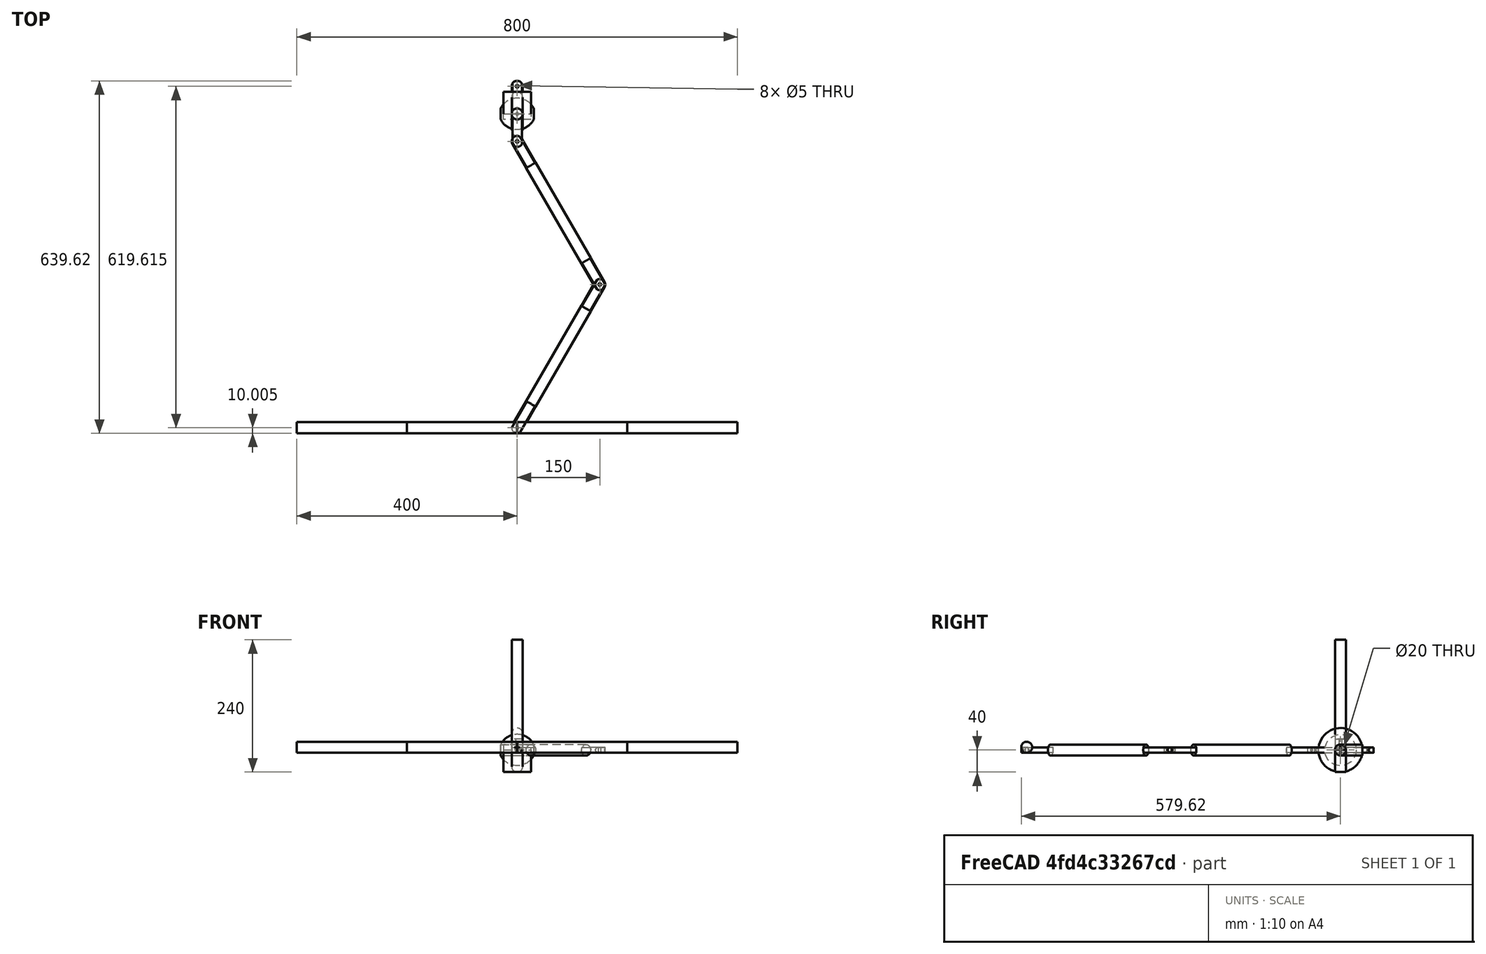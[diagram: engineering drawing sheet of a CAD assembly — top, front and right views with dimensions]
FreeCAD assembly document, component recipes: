
FREECAD ASSEMBLY — COMPONENT RECIPES ("Demo9Rev-Trans")

This assembly document has 7 components, labeled P0..P6 below (a component is one placed body or linked part). 7 of them carry a construction recipe — the FreeCAD feature program that regenerates the part from scratch, quoted from this document or its linked companion documents; the rest are supplied as boundary geometry only. No exploded tour is included for this assembly.
COMPONENT P0 — recipe-attached ("Weight", modeled in this document).
Construction recipe (the document's own serialized feature program — sketch geometry with constraints, then the solid features built on it; lengths are millimeters unless a unit is written):

FEATURE [Sketcher::SketchObject] Sketch
  FullyConstrained = true
  MapMode = 5
  Support = -> [XY_Plane]
  sketch-geometry (2):
    g0: LineSegment StartX=-30 StartY=10 StartZ=0 EndX=30 EndY=10 EndZ=0
    g1: ArcOfCircle CenterX=0 CenterY=-5 CenterZ=0 NormalX=0 NormalY=0 NormalZ=1 AngleXU=0 Radius=33.541 StartAngle=0.463648 EndAngle=2.67795
  constraints (7):
    c: Horizontal(g0)
    c: DistanceY(g-1,g0) = 10
    c: DistanceX(g-1,g0) = 30
    c: PointOnObject(g1,g-2)
    c: DistanceY(g1,g-1) = 5
    c: Coincident(g1,g0)
    c: Coincident(g1,g0)
FEATURE [PartDesign::Revolution] Revolution
  Angle = 360
  Axis = (1,0,0)
  Base = (0,0,0)
  Profile = -> Sketch
  ReferenceAxis = -> Sketch [H_Axis]
FEATURE [PartDesign::CoordinateSystem] WeightTop
  AttacherType = Attacher::AttachEngine3D
  MapMode = 11
  Placement = pos=(30,-1.8e-15,0) rot=(0.707107,0,0.707107;3.14159rad)
  Support = -> [Revolution]
FEATURE [PartDesign::CoordinateSystem] WeightBot
  AttacherType = Attacher::AttachEngine3D
  MapMode = 11
  Placement = pos=(-30,0,0) rot=(0.707107,0,0.707107;3.14159rad)
  Support = -> [Revolution]
FEATURE [PartDesign::CoordinateSystem] WeightLCS
  AttacherType = Attacher::AttachEngine3D
  MapMode = 2
  Support = -> [Body003]
FEATURE [PartDesign::Body] Body  label="Weight"
  Group = -> [Sketch,Revolution,WeightLCS,WeightTop,WeightBot]
  Origin = -> Origin
  Tip = -> Revolution
COMPONENT P1 — recipe-attached ("Rod", modeled in this document).
Construction recipe (the document's own serialized feature program — sketch geometry with constraints, then the solid features built on it; lengths are millimeters unless a unit is written):

FEATURE [Sketcher::SketchObject] Sketch001
  FullyConstrained = true
  MapMode = 5
  Support = -> [XY_Plane001]
  sketch-geometry (1):
    g0: Circle CenterX=0 CenterY=0 CenterZ=0 NormalX=0 NormalY=0 NormalZ=1 AngleXU=0 Radius=10
  constraints (2):
    c: Coincident(g0,g-1)
    c: Diameter(g0) = 20
FEATURE [PartDesign::Pad] Pad
  Direction = (0,0,1)
  Length = 200
  Length2 = 10
  Profile = -> Sketch001
  ReferenceAxis = -> Sketch001 [N_Axis]
  Type = 0
FEATURE [PartDesign::CoordinateSystem] RodTop
  AttacherType = Attacher::AttachEngine3D
  MapMode = 11
  Placement = pos=(0,0,200) rot=(0,0,1;1.5708rad)
  Support = -> [Pad]
FEATURE [PartDesign::CoordinateSystem] RodBottom
  AttacherType = Attacher::AttachEngine3D
  MapMode = 11
  Placement = pos=(0,0,0) rot=(0,0,1;1.5708rad)
  Support = -> [Pad]
FEATURE [PartDesign::Body] Body001  label="Rod"
  Group = -> [Sketch001,Pad,RodTop,RodBottom]
  Origin = -> Origin001
  Tip = -> Pad
COMPONENT P2 — recipe-attached ("LugBody", modeled in this document).
Construction recipe (the document's own serialized feature program — sketch geometry with constraints, then the solid features built on it; lengths are millimeters unless a unit is written):

FEATURE [Sketcher::SketchObject] Sketch002
  FullyConstrained = true
  MapMode = 5
  Support = -> [XY_Plane002]
  sketch-geometry (5):
    g0: LineSegment StartX=-10 StartY=0 StartZ=0 EndX=-10 EndY=50 EndZ=0
    g1: ArcOfCircle CenterX=0 CenterY=50 CenterZ=0 NormalX=0 NormalY=0 NormalZ=1 AngleXU=0 Radius=10 StartAngle=1e-16 EndAngle=3.14159
    g2: LineSegment StartX=10 StartY=50 StartZ=0 EndX=10 EndY=0 EndZ=0
    g3: LineSegment StartX=10 StartY=0 StartZ=0 EndX=-10 EndY=0 EndZ=0
    g4: Circle CenterX=0 CenterY=50 CenterZ=0 NormalX=0 NormalY=0 NormalZ=1 AngleXU=0 Radius=2.5
  constraints (13):
    c: PointOnObject(g0,g-1)
    c: Vertical(g0)
    c: Tangent(g0,g1) = 1.5708
    c: Tangent(g1,g2) = 1.5708
    c: Coincident(g2,g3)
    c: Coincident(g3,g0)
    c: Horizontal(g3)
    c: PointOnObject(g1,g-2)
    c: Vertical(g2)
    c: Diameter(g1) = 20
    c: Distance(g2) = 50
    c: Coincident(g4,g1)
    c: Diameter(g4) = 5
FEATURE [PartDesign::Pad] Pad001
  Direction = (0,0,1)
  Length = 10
  Length2 = 10
  Midplane = true
  Profile = -> Sketch002
  ReferenceAxis = -> Sketch002 [N_Axis]
  Type = 0
FEATURE [PartDesign::Body] Body002  label="LugBody"
  Group = -> [Sketch002,Pad001]
  Origin = -> Origin002
  Tip = -> Pad001
COMPONENT P3 — recipe-attached ("LugCylinder", modeled in this document).
Construction recipe (the document's own serialized feature program — sketch geometry with constraints, then the solid features built on it; lengths are millimeters unless a unit is written):

FEATURE [Sketcher::SketchObject] Sketch003
  FullyConstrained = true
  MapMode = 5
  Placement = pos=(0,0,0) rot=(1,0,0;1.5708rad)
  Support = -> [XZ_Plane003]
  sketch-geometry (1):
    g0: Circle CenterX=0 CenterY=0 CenterZ=0 NormalX=0 NormalY=0 NormalZ=1 AngleXU=0 Radius=10
  constraints (2):
    c: Coincident(g0,g-1)
    c: Diameter(g0) = 20
FEATURE [PartDesign::Pad] Pad002
  Direction = (0,-1,-2e-16)
  Length = 60
  Length2 = 10
  Placement = pos=(0,0,0) rot=(1,0,0;1.5708rad)
  Profile = -> Sketch003
  ReferenceAxis = -> Sketch003 [N_Axis]
  Reversed = true
  Type = 0
FEATURE [PartDesign::Boolean] Boolean
  BaseFeature = -> Pad002
  Group = -> [Body002]
  Type = 2
FEATURE [PartDesign::CoordinateSystem] LugHole
  AttacherType = Attacher::AttachEngine3D
  MapMode = 11
  Placement = pos=(0,50,5) rot=(0,0,1;1.5708rad)
  Support = -> [Boolean]
FEATURE [PartDesign::CoordinateSystem] LugFace
  AttacherType = Attacher::AttachEngine3D
  MapMode = 5
  Placement = pos=(0,0,0) rot=(1,0,0;1.5708rad)
  Support = -> [Boolean]
FEATURE [PartDesign::CoordinateSystem] LugRot30
  AttacherType = Attacher::AttachEngine3D
  AttachmentOffset = pos=(0,0,0) rot=(0,0,1;0.523599rad)
  MapMode = 11
  Placement = pos=(0,50,5) rot=(0,0,1;2.0944rad)
  Support = -> [Boolean]
FEATURE [PartDesign::CoordinateSystem] LugRot60
  AttacherType = Attacher::AttachEngine3D
  AttachmentOffset = pos=(0,0,0) rot=(0,0,1;1.0472rad)
  MapMode = 11
  Placement = pos=(0,50,5) rot=(0,0,1;2.61799rad)
  Support = -> [Boolean]
FEATURE [PartDesign::Body] Body003  label="LugCylinder"
  Group = -> [Sketch003,Pad002,Boolean,LugHole,LugFace,LugRot30,LugRot60]
  Origin = -> Origin003
  Tip = -> Boolean
COMPONENT P4 — recipe-attached ("BobBody", modeled in this document).
Construction recipe (the document's own serialized feature program — sketch geometry with constraints, then the solid features built on it; lengths are millimeters unless a unit is written):

FEATURE [Sketcher::SketchObject] Sketch004
  FullyConstrained = true
  MapMode = 5
  Support = -> [XY_Plane004]
  sketch-geometry (4):
    g0: LineSegment StartX=-10 StartY=0 StartZ=0 EndX=-10 EndY=30 EndZ=0
    g1: ArcOfCircle CenterX=0 CenterY=30 CenterZ=0 NormalX=0 NormalY=0 NormalZ=1 AngleXU=0 Radius=10 StartAngle=2e-16 EndAngle=3.14159
    g2: LineSegment StartX=10 StartY=30 StartZ=0 EndX=10 EndY=0 EndZ=0
    g3: LineSegment StartX=10 StartY=0 StartZ=0 EndX=-10 EndY=0 EndZ=0
  constraints (11):
    c: PointOnObject(g0,g-1)
    c: Vertical(g0)
    c: Tangent(g0,g1) = 1.5708
    c: Tangent(g1,g2) = 1.5708
    c: Coincident(g2,g3)
    c: Coincident(g3,g0)
    c: Vertical(g2)
    c: PointOnObject(g1,g-2)
    c: Diameter(g1) = 20
    c: Distance(g0) = 30
    c: PointOnObject(g2,g-1)
FEATURE [PartDesign::Revolution] Revolution001
  Angle = 360
  Axis = (1,0,0)
  Base = (0,0,0)
  Profile = -> Sketch004
  ReferenceAxis = -> Sketch004 [H_Axis]
FEATURE [PartDesign::CoordinateSystem] BobBody  label="BobBody001"
  AttacherType = Attacher::AttachEngine3D
  MapMode = 11
  Placement = pos=(-10,0,0) rot=(0.707107,0,0.707107;3.14159rad)
  Support = -> [Revolution001]
FEATURE [PartDesign::Body] Body004  label="BobBody"
  Group = -> [Sketch004,Revolution001,BobBody]
  Origin = -> Origin004
  Tip = -> Revolution001
COMPONENT P5 — recipe-attached ("GroundBody", modeled in this document).
Construction recipe (the document's own serialized feature program — sketch geometry with constraints, then the solid features built on it; lengths are millimeters unless a unit is written):

FEATURE [Sketcher::SketchObject] Sketch005
  FullyConstrained = true
  MapMode = 5
  Support = -> [XY_Plane005]
  sketch-geometry (4):
    g0: LineSegment StartX=-25 StartY=10 StartZ=0 EndX=25 EndY=10 EndZ=0
    g1: LineSegment StartX=25 StartY=10 StartZ=0 EndX=25 EndY=-10 EndZ=0
    g2: LineSegment StartX=25 StartY=-10 StartZ=0 EndX=-25 EndY=-10 EndZ=0
    g3: LineSegment StartX=-25 StartY=-10 StartZ=0 EndX=-25 EndY=10 EndZ=0
  constraints (11):
    c: Coincident(g0,g1)
    c: Coincident(g1,g2)
    c: Coincident(g2,g3)
    c: Coincident(g3,g0)
    c: Horizontal(g0)
    c: Horizontal(g2)
    c: Vertical(g1)
    c: Vertical(g3)
    c: DistanceY(g2,g0) = 20
    c: DistanceX(g0,g0) = 50
    c: Symmetric(g0,g1,g-1)
FEATURE [PartDesign::Pad] Pad003
  Direction = (0,0,1)
  Length = 40
  Length2 = 10
  Profile = -> Sketch005
  ReferenceAxis = -> Sketch005 [N_Axis]
  Reversed = true
  Type = 0
FEATURE [PartDesign::CoordinateSystem] GroundLCS
  AttacherType = Attacher::AttachEngine3D
  MapMode = 5
  Placement = pos=(0,0,-40) rot=(1,0,0;3.14159rad)
  Support = -> [Pad003]
FEATURE [PartDesign::Body] Body005  label="GroundBody"
  Group = -> [Sketch005,Pad003,GroundLCS]
  Origin = -> Origin005
  Tip = -> Pad003
COMPONENT P6 — recipe-attached ("Spacer", modeled in this document).
Construction recipe (the document's own serialized feature program — sketch geometry with constraints, then the solid features built on it; lengths are millimeters unless a unit is written):

FEATURE [Sketcher::SketchObject] Sketch006
  FullyConstrained = true
  MapMode = 5
  Support = -> [XY_Plane007]
  sketch-geometry (2):
    g0: Circle CenterX=0 CenterY=0 CenterZ=0 NormalX=0 NormalY=0 NormalZ=1 AngleXU=0 Radius=10
    g1: Circle CenterX=0 CenterY=0 CenterZ=0 NormalX=0 NormalY=0 NormalZ=1 AngleXU=0 Radius=2.5
  constraints (4):
    c: Coincident(g0,g-1)
    c: Coincident(g1,g0)
    c: Diameter(g0) = 20
    c: Diameter(g1) = 5
FEATURE [PartDesign::Pad] Pad004
  Direction = (0,0,1)
  Length = 20
  Length2 = 10
  Profile = -> Sketch006
  ReferenceAxis = -> Sketch006 [N_Axis]
  Type = 0
FEATURE [PartDesign::CoordinateSystem] SpacerTop
  AttacherType = Attacher::AttachEngine3D
  MapMode = 11
  Placement = pos=(0,0,20) rot=(0,0,1;1.5708rad)
  Support = -> [Pad004]
FEATURE [PartDesign::Body] Body006  label="Spacer"
  Group = -> [Sketch006,Pad004,SpacerTop]
  Origin = -> Origin007
  Tip = -> Pad004
PROVENANCE & LICENSES
A FreeCAD (.FCStd) document from a public repository crawl; recipes are the document's own serialized feature recipes (and, for linked parts, companion documents' recipes).
License: gpl-3.0.
